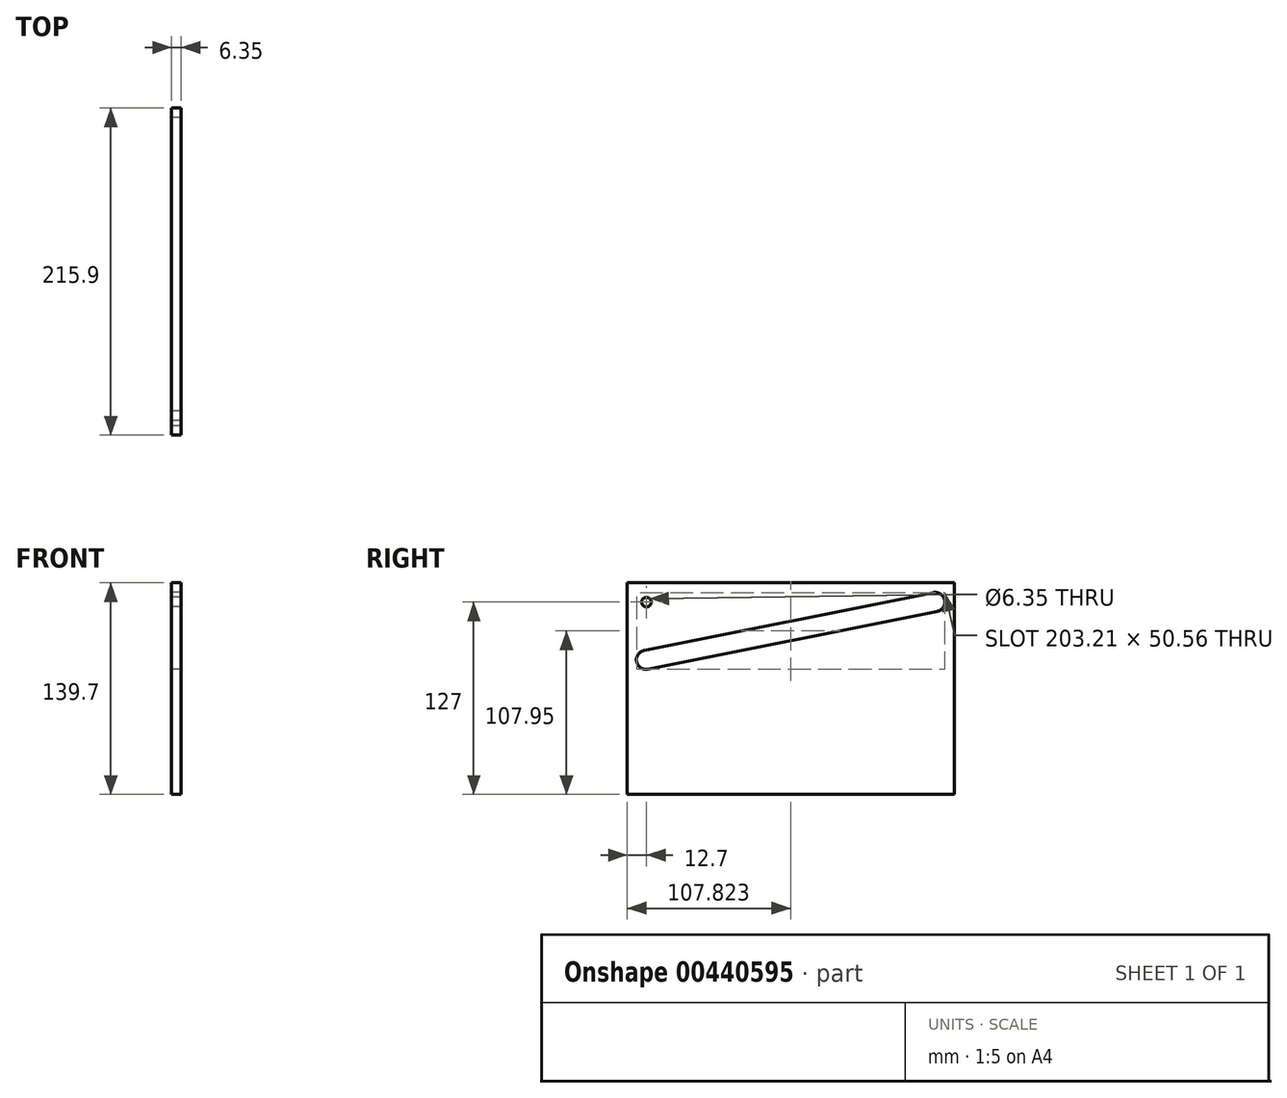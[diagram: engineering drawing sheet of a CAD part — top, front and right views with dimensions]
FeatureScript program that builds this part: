
annotation { "Feature Type Name" : "Feature", "Feature Type Description" : "" }
export const myFeature = defineFeature(function(context is Context, id is Id, definition is map)
    precondition{}
    {
        {
            var Q0;
            Q0=qCreatedBy(makeId("Right.planeOp"),FACE);
            var sketch = newSketch(context, id + "F0", { "sketchPlane" : qUnion([Q0])});
            skLineSegment(sketch, "E0.bottom", {"start": v(0, 0) * mm, "end": v(215.9, 0) * mm});
            skLineSegment(sketch, "E0.top", {"start": v(0, 139.7) * mm, "end": v(215.9, 139.7) * mm});
            skLineSegment(sketch, "E0.left", {"start": v(0, 0) * mm, "end": v(0, 139.7) * mm});
            skLineSegment(sketch, "E0.right", {"start": v(215.9, 0) * mm, "end": v(215.9, 139.7) * mm});
            skCircle(sketch, "E1", {"center": v(12.7, 127) * mm, "radius": 3.18 * mm});
            skArc(sketch, "E2.0.startCap", {"start": v(13.69, 82.67) * mm, "mid": v(6.22, 87.66) * mm, "end": v(11.2, 95.13) * mm});
            skArc(sketch, "E2.0.endCap", {"start": v(201.96, 133.23) * mm, "mid": v(209.43, 128.24) * mm, "end": v(204.44, 120.77) * mm});
            skLineSegment(sketch, "E3", {"start": v(11.2, 95.13) * mm, "end": v(201.96, 133.23) * mm});
            skLineSegment(sketch, "E4", {"start": v(204.44, 120.77) * mm, "end": v(13.69, 82.67) * mm});
            skSolve(sketch);
        }
        {
            var Q0;
            Q0=makeQuery(id+"F0.imprint","IMPRINT",FACE,{"disambiguationData":[TD([[makeQuery(id+"F0.imprint","IMPRINT",EDGE,{"derivedFrom":sQuery(id+"F0.wireOp",EDGE,"E0.bottom")}),1.0]])]});
            extrude(context, id + "F1", {"entities" : qUnion([Q0]), "depth" : 6.35 * mm});
        }
    });
